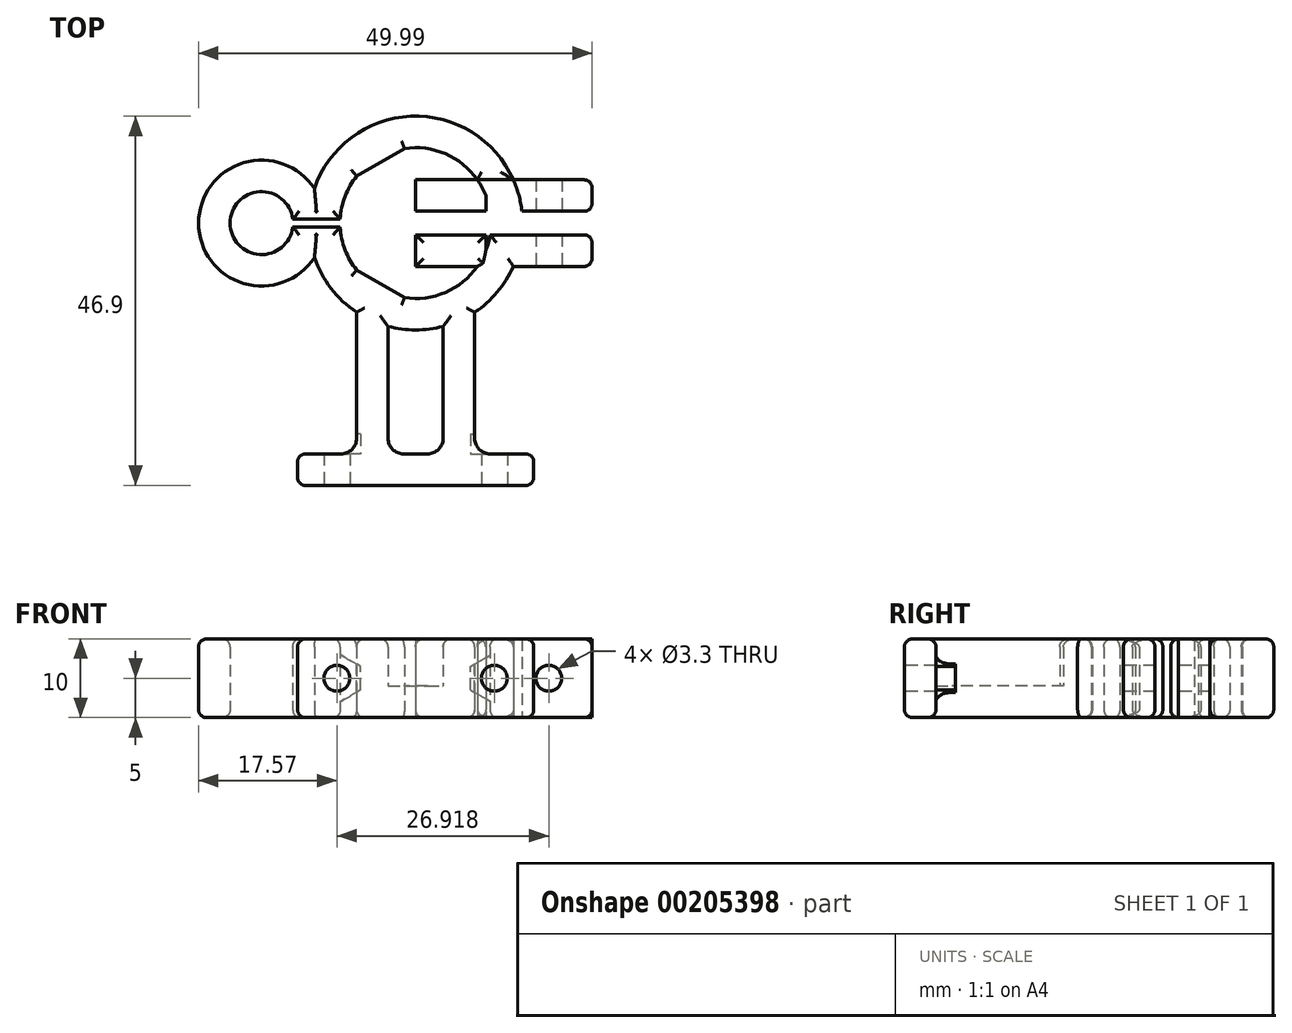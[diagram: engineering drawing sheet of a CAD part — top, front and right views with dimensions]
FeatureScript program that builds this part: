
annotation { "Feature Type Name" : "Feature", "Feature Type Description" : "" }
export const myFeature = defineFeature(function(context is Context, id is Id, definition is map)
    precondition{}
    {
        {
            assignVariable(context, id + "F0", {"name" : "wallWidth", "anyValue" : 4});
        }
        {
            assignVariable(context, id + "F1", {"name" : "height", "anyValue" : 10});
        }
        {
            var Q0;
            Q0=qCreatedBy(makeId("Top.planeOp"),FACE);
            var sketch = newSketch(context, id + "F2", { "sketchPlane" : qUnion([Q0])});
            skCircle(sketch, "E0", {"center": v(0, 0) * mm, "radius": 9.58 * mm});
            skPoint(sketch, "E1", {"position": v(0, 9.58) * mm});
            skPoint(sketch, "E2", {"position": v(-4.46, -7.72) * mm});
            skLineSegment(sketch, "E3", {"start": v(0, 9.58) * mm, "end": v(0, -8.92) * mm, "construction": true});
            skLineSegment(sketch, "E4.2.0", {"start": v(-7.5, -5.97) * mm, "end": v(-1.43, -9.47) * mm});
            skLineSegment(sketch, "E5.1.0", {"start": v(-1.43, 9.47) * mm, "end": v(-7.5, 5.97) * mm});
            skLineSegment(sketch, "E5.2.0", {"start": v(8.92, -3.5) * mm, "end": v(8.92, 3.5) * mm});
            skLineSegment(sketch, "E5.anchor1", {"start": v(0, 0) * mm, "end": v(-7.5, -5.97) * mm, "construction": true});
            skLineSegment(sketch, "E5.anchor2", {"start": v(0, 0) * mm, "end": v(8.92, -3.5) * mm, "construction": true});
            skCircle(sketch, "E6.0", {"center": v(0, 0) * mm, "radius": 13.58 * mm});
            skLineSegment(sketch, "E7.bottom", {"start": v(7.5, -11.32) * mm, "end": v(-7.5, -11.32) * mm});
            skLineSegment(sketch, "E7.top", {"start": v(1.5, -29.32) * mm, "end": v(-1.5, -29.32) * mm});
            skLineSegment(sketch, "E7.left", {"start": v(7.5, -11.32) * mm, "end": v(7.5, -27.32) * mm});
            skLineSegment(sketch, "E7.right", {"start": v(-7.5, -11.32) * mm, "end": v(-7.5, -27.32) * mm});
            skPoint(sketch, "E7.middle", {"position": v(0, -20.32) * mm});
            skLineSegment(sketch, "E8.bottom", {"start": v(-9.5, -29.32) * mm, "end": v(-14, -29.32) * mm});
            skLineSegment(sketch, "E8.top", {"start": v(14, -33.32) * mm, "end": v(-14, -33.32) * mm});
            skLineSegment(sketch, "E8.left", {"start": v(15, -30.32) * mm, "end": v(15, -32.32) * mm});
            skLineSegment(sketch, "E8.right", {"start": v(-15, -30.32) * mm, "end": v(-15, -32.32) * mm});
            skPoint(sketch, "E8.middle", {"position": v(0, -31.32) * mm});
            skPoint(sketch, "E9", {"position": v(0, -33.32) * mm});
            skLineSegment(sketch, "E10", {"start": v(0, -33.32) * mm, "end": v(10, -33.32) * mm});
            skLineSegment(sketch, "E11", {"start": v(0, -33.32) * mm, "end": v(-10, -33.32) * mm});
            skLineSegment(sketch, "E12", {"start": v(0, 0) * mm, "end": v(13.58, 0) * mm, "construction": true});
            skLineSegment(sketch, "E13.bottom", {"start": v(0, 0) * mm, "end": v(18.62, 0) * mm});
            skLineSegment(sketch, "E13.top", {"start": v(0, 1.5) * mm, "end": v(18.62, 1.5) * mm});
            skLineSegment(sketch, "E13.left", {"start": v(0, 0) * mm, "end": v(0, 1.5) * mm});
            skLineSegment(sketch, "E13.right", {"start": v(18.62, 0) * mm, "end": v(18.62, 1.5) * mm});
            skLineSegment(sketch, "E14.bottom", {"start": v(0, 0) * mm, "end": v(18.6, 0) * mm});
            skLineSegment(sketch, "E14.top", {"start": v(0, -1.5) * mm, "end": v(18.6, -1.5) * mm});
            skLineSegment(sketch, "E14.left", {"start": v(0, 0) * mm, "end": v(0, -1.5) * mm});
            skLineSegment(sketch, "E14.right", {"start": v(18.6, 0) * mm, "end": v(18.6, -1.5) * mm});
            skLineSegment(sketch, "E15.bottom", {"start": v(0, 1.5) * mm, "end": v(21.42, 1.5) * mm});
            skLineSegment(sketch, "E15.top", {"start": v(0, 5.5) * mm, "end": v(21.42, 5.5) * mm});
            skLineSegment(sketch, "E15.left", {"start": v(0, 1.5) * mm, "end": v(0, 5.5) * mm});
            skLineSegment(sketch, "E15.right", {"start": v(22.42, 2.5) * mm, "end": v(22.42, 4.5) * mm});
            skLineSegment(sketch, "E16.bottom", {"start": v(0, -1.5) * mm, "end": v(21.42, -1.5) * mm});
            skLineSegment(sketch, "E16.top", {"start": v(0, -5.5) * mm, "end": v(21.42, -5.5) * mm});
            skLineSegment(sketch, "E16.left", {"start": v(0, -1.5) * mm, "end": v(0, -5.5) * mm});
            skLineSegment(sketch, "E16.right", {"start": v(22.42, -2.5) * mm, "end": v(22.42, -4.5) * mm});
            skLineSegment(sketch, "E17", {"start": v(0, 0) * mm, "end": v(-19.57, 0) * mm, "construction": true});
            skCircle(sketch, "E18", {"center": v(-19.57, 0) * mm, "radius": 4 * mm});
            skCircle(sketch, "E19.0", {"center": v(-19.57, 0) * mm, "radius": 8 * mm});
            skLineSegment(sketch, "E20.left", {"start": v(-19.57, 8) * mm, "end": v(-19.57, 2.68) * mm});
            skLineSegment(sketch, "E21", {"start": v(-19.57, 0) * mm, "end": v(-19.57, 8) * mm, "construction": true});
            skLineSegment(sketch, "E22", {"start": v(3.5, -11.32) * mm, "end": v(3.5, -27.32) * mm});
            skLineSegment(sketch, "E23", {"start": v(-3.5, -11.32) * mm, "end": v(-3.5, -27.32) * mm});
            skLineSegment(sketch, "E24.top", {"start": v(-19.57, 0.5) * mm, "end": v(-9.57, 0.5) * mm});
            skLineSegment(sketch, "E24.right", {"start": v(-9.57, 0) * mm, "end": v(-9.57, 0.5) * mm});
            skLineSegment(sketch, "E25.top", {"start": v(-18.57, -0.5) * mm, "end": v(-9.57, -0.5) * mm});
            skLineSegment(sketch, "E25.right", {"start": v(-9.57, 0) * mm, "end": v(-9.57, -0.5) * mm});
            skPoint(sketch, "E26", {"position": v(-15.57, 0) * mm});
            skPoint(sketch, "E27.newPointB", {"position": v(15, -29.32) * mm});
            skLineSegment(sketch, "E28", {"start": v(14, -29.32) * mm, "end": v(9.5, -29.32) * mm});
            skPoint(sketch, "E29.visualSharp", {"position": v(7.5, -29.32) * mm});
            skArc(sketch, "E29.filletArc", {"start": v(7.5, -27.32) * mm, "mid": v(8.09, -28.74) * mm, "end": v(9.5, -29.32) * mm});
            skPoint(sketch, "E30.newPointA", {"position": v(3.5, -29.32) * mm});
            skArc(sketch, "E30.filletArc", {"start": v(1.5, -29.32) * mm, "mid": v(2.91, -28.74) * mm, "end": v(3.5, -27.32) * mm});
            skPoint(sketch, "E31.newPointA", {"position": v(-7.5, -29.32) * mm});
            skPoint(sketch, "E31.newPointB", {"position": v(-3.5, -29.32) * mm});
            skArc(sketch, "E31.filletArc", {"start": v(-3.5, -27.32) * mm, "mid": v(-2.91, -28.74) * mm, "end": v(-1.5, -29.32) * mm});
            skArc(sketch, "E32.filletArc", {"start": v(-9.5, -29.32) * mm, "mid": v(-8.09, -28.74) * mm, "end": v(-7.5, -27.32) * mm});
            skPoint(sketch, "E33.visualSharp", {"position": v(22.42, -1.5) * mm});
            skArc(sketch, "E33.filletArc", {"start": v(22.42, -2.5) * mm, "mid": v(22.12, -1.8) * mm, "end": v(21.42, -1.5) * mm});
            skPoint(sketch, "E34.visualSharp", {"position": v(22.42, 1.5) * mm});
            skArc(sketch, "E34.filletArc", {"start": v(21.42, 1.5) * mm, "mid": v(22.12, 1.8) * mm, "end": v(22.42, 2.5) * mm});
            skPoint(sketch, "E35.visualSharp", {"position": v(22.42, 5.5) * mm});
            skArc(sketch, "E35.filletArc", {"start": v(22.42, 4.5) * mm, "mid": v(22.12, 5.2) * mm, "end": v(21.42, 5.5) * mm});
            skPoint(sketch, "E36.visualSharp", {"position": v(22.42, -5.5) * mm});
            skArc(sketch, "E36.filletArc", {"start": v(21.42, -5.5) * mm, "mid": v(22.12, -5.2) * mm, "end": v(22.42, -4.5) * mm});
            skArc(sketch, "E37.filletArc", {"start": v(15, -30.32) * mm, "mid": v(14.7, -29.62) * mm, "end": v(14, -29.32) * mm});
            skPoint(sketch, "E38.visualSharp", {"position": v(15, -33.32) * mm});
            skArc(sketch, "E38.filletArc", {"start": v(14, -33.32) * mm, "mid": v(14.7, -33.03) * mm, "end": v(15, -32.32) * mm});
            skPoint(sketch, "E39", {"position": v(12.42, -5.5) * mm});
            skPoint(sketch, "E40", {"position": v(12.42, 5.5) * mm});
            skPoint(sketch, "E41.visualSharp", {"position": v(-15, -33.32) * mm});
            skArc(sketch, "E41.filletArc", {"start": v(-15, -32.32) * mm, "mid": v(-14.7, -33.03) * mm, "end": v(-14, -33.32) * mm});
            skPoint(sketch, "E42.visualSharp", {"position": v(-15, -29.32) * mm});
            skArc(sketch, "E42.filletArc", {"start": v(-14, -29.32) * mm, "mid": v(-14.7, -29.62) * mm, "end": v(-15, -30.32) * mm});
            skLineSegment(sketch, "E43", {"start": v(3.5, -29.32) * mm, "end": v(3.5, -27.32) * mm, "construction": true});
            skLineSegment(sketch, "E44", {"start": v(-3.5, -29.32) * mm, "end": v(-3.5, -27.32) * mm, "construction": true});
            skLineSegment(sketch, "E45", {"start": v(9.5, -29.32) * mm, "end": v(-9.5, -29.32) * mm, "construction": true});
            skLineSegment(sketch, "E46", {"start": v(7.5, -27.32) * mm, "end": v(7.5, -29.32) * mm, "construction": true});
            skSolve(sketch);
        }
        {
            var Q0;
            {var subQ6=sQuery(id+"F2.wireOp",EDGE,"E20.right");Q0=makeQuery(id+"F2.imprint","IMPRINT",FACE,{"disambiguationData":[TD([[makeQuery(id+"F2.imprint","IMPRINT",EDGE,{"derivedFrom":subQ6}),1.0]])]});}
            var Q1;
            {var subQ0=sQuery(id+"F2.wireOp",EDGE,"E15.bottom");var subQ1=sQuery(id+"F2.wireOp",EDGE,"E0");var subQ2=makeQuery(id+"F2.imprint","INTERSECT",VERTEX,{"derivedFrom":[subQ1,subQ0]});Q1=makeQuery(id+"F2.imprint","IMPRINT",FACE,{"disambiguationData":[TD([[makeQuery(id+"F2.imprint","IMPRINT",EDGE,{"disambiguationData":[TD([[subQ2,-1.0]])],"derivedFrom":subQ1}),-1.0]])]});}
            var Q2;
            {var subQ2=sQuery(id+"F2.wireOp",EDGE,"E15.right");Q2=makeQuery(id+"F2.imprint","IMPRINT",FACE,{"disambiguationData":[TD([[makeQuery(id+"F2.imprint","IMPRINT",EDGE,{"derivedFrom":subQ2}),1.0]])]});}
            var Q3;
            {var subQ0=sQuery(id+"F2.wireOp",EDGE,"E16.right");Q3=makeQuery(id+"F2.imprint","IMPRINT",FACE,{"disambiguationData":[TD([[makeQuery(id+"F2.imprint","IMPRINT",EDGE,{"derivedFrom":subQ0}),-1.0]])]});}
            var Q4;
            {var subQ0=sQuery(id+"F2.wireOp",EDGE,"E16.top");var subQ1=sQuery(id+"F2.wireOp",EDGE,"E0");var subQ2=makeQuery(id+"F2.imprint","INTERSECT",VERTEX,{"derivedFrom":[subQ1,subQ0]});Q4=makeQuery(id+"F2.imprint","IMPRINT",FACE,{"disambiguationData":[TD([[makeQuery(id+"F2.imprint","IMPRINT",EDGE,{"disambiguationData":[TD([[subQ2,-1.0]])],"derivedFrom":subQ1}),-1.0]])]});}
            var Q5;
            {var subQ0=sQuery(id+"F2.wireOp",EDGE,"vKI5tk8C-QuSu-6IvA-wCT6-3tnONTHLCrgP.right");Q5=makeQuery(id+"F2.imprint","IMPRINT",FACE,{"disambiguationData":[TD([[makeQuery(id+"F2.imprint","IMPRINT",EDGE,{"derivedFrom":subQ0}),1.0]])]});}
            var Q6;
            {var subQ0=sQuery(id+"F2.wireOp",EDGE,"E20.right");Q6=makeQuery(id+"F2.imprint","IMPRINT",FACE,{"disambiguationData":[TD([[makeQuery(id+"F2.imprint","IMPRINT",EDGE,{"derivedFrom":subQ0}),-1.0]])]});}
            var Q7;
            {var subQ0=sQuery(id+"F2.wireOp",EDGE,"vKI5tk8C-QuSu-6IvA-wCT6-3tnONTHLCrgP.right");Q7=makeQuery(id+"F2.imprint","IMPRINT",FACE,{"disambiguationData":[TD([[makeQuery(id+"F2.imprint","IMPRINT",EDGE,{"derivedFrom":subQ0}),-1.0]])]});}
            var Q8;
            {var subQ0=sQuery(id+"F2.wireOp",EDGE,"E5.1.0");Q8=makeQuery(id+"F2.imprint","IMPRINT",FACE,{"disambiguationData":[TD([[makeQuery(id+"F2.imprint","IMPRINT",EDGE,{"derivedFrom":subQ0}),-1.0]])]});}
            var Q9;
            {var subQ0=sQuery(id+"F2.wireOp",EDGE,"E15.bottom");var subQ1=sQuery(id+"F2.wireOp",EDGE,"E0");var subQ2=makeQuery(id+"F2.imprint","INTERSECT",VERTEX,{"derivedFrom":[subQ1,subQ0]});Q9=makeQuery(id+"F2.imprint","IMPRINT",FACE,{"disambiguationData":[TD([[makeQuery(id+"F2.imprint","IMPRINT",EDGE,{"disambiguationData":[TD([[subQ2,-1.0]])],"derivedFrom":subQ1}),1.0]])]});}
            var Q10;
            {var subQ0=sQuery(id+"F2.wireOp",EDGE,"E5.2.0");var subQ1=sQuery(id+"F2.wireOp",EDGE,"E0");var subQ2=makeQuery(id+"F2.imprint","INTERSECT",VERTEX,{"disambiguationData":[OD(1.0)],"derivedFrom":[subQ1,subQ0]});Q10=makeQuery(id+"F2.imprint","IMPRINT",FACE,{"disambiguationData":[TD([[makeQuery(id+"F2.imprint","IMPRINT",EDGE,{"disambiguationData":[TD([[subQ2,1.0]])],"derivedFrom":subQ1}),1.0]])]});}
            var Q11;
            {var subQ0=sQuery(id+"F2.wireOp",EDGE,"E4.2.0");Q11=makeQuery(id+"F2.imprint","IMPRINT",FACE,{"disambiguationData":[TD([[makeQuery(id+"F2.imprint","IMPRINT",EDGE,{"derivedFrom":subQ0}),-1.0]])]});}
            var Q12;
            {var subQ0=sQuery(id+"F2.wireOp",EDGE,"E7.bottom");var subQ3=sQuery(id+"F2.wireOp",EDGE,"E22");var subQ5=makeQuery(id+"F2.imprint","INTERSECT",VERTEX,{"derivedFrom":[subQ0,subQ3]});Q12=makeQuery(id+"F2.imprint","IMPRINT",FACE,{"disambiguationData":[TD([[makeQuery(id+"F2.imprint","IMPRINT",EDGE,{"disambiguationData":[TD([[subQ5,-1.0]])],"derivedFrom":subQ3}),1.0]])]});}
            var Q13;
            {var subQ0=sQuery(id+"F2.wireOp",EDGE,"E23");var subQ1=sQuery(id+"F2.wireOp",EDGE,"E6.0");var subQ2=makeQuery(id+"F2.imprint","INTERSECT",VERTEX,{"derivedFrom":[subQ1,subQ0]});Q13=makeQuery(id+"F2.imprint","IMPRINT",FACE,{"disambiguationData":[TD([[makeQuery(id+"F2.imprint","IMPRINT",EDGE,{"disambiguationData":[TD([[subQ2,-1.0]])],"derivedFrom":subQ1}),1.0]])]});}
            var Q14;
            {var subQ0=sQuery(id+"F2.wireOp",EDGE,"E23");var subQ1=sQuery(id+"F2.wireOp",EDGE,"E6.0");var subQ2=makeQuery(id+"F2.imprint","INTERSECT",VERTEX,{"derivedFrom":[subQ1,subQ0]});Q14=makeQuery(id+"F2.imprint","IMPRINT",FACE,{"disambiguationData":[TD([[makeQuery(id+"F2.imprint","IMPRINT",EDGE,{"disambiguationData":[TD([[subQ2,-1.0]])],"derivedFrom":subQ1}),1.0]])]});}
            var Q15;
            {var subQ0=sQuery(id+"F2.wireOp",EDGE,"E7.bottom");var subQ3=sQuery(id+"F2.wireOp",EDGE,"E23");var subQ5=makeQuery(id+"F2.imprint","INTERSECT",VERTEX,{"derivedFrom":[subQ0,subQ3]});Q15=makeQuery(id+"F2.imprint","IMPRINT",FACE,{"disambiguationData":[TD([[makeQuery(id+"F2.imprint","IMPRINT",EDGE,{"disambiguationData":[TD([[subQ5,-1.0]])],"derivedFrom":subQ3}),-1.0]])]});}
            var Q16;
            {var subQ4=sQuery(id+"F2.wireOp",EDGE,"E7.left");Q16=makeQuery(id+"F2.imprint","IMPRINT",FACE,{"disambiguationData":[TD([[makeQuery(id+"F2.imprint","IMPRINT",EDGE,{"derivedFrom":subQ4}),-1.0]])]});}
            var Q17;
            {var subQ4=sQuery(id+"F2.wireOp",EDGE,"E7.right");Q17=makeQuery(id+"F2.imprint","IMPRINT",FACE,{"disambiguationData":[TD([[makeQuery(id+"F2.imprint","IMPRINT",EDGE,{"derivedFrom":subQ4}),1.0]])]});}
            var Q18;
            Q18=makeQuery(id+"F2.imprint","IMPRINT",FACE,{"disambiguationData":[TD([[makeQuery(id+"F2.imprint","IMPRINT",EDGE,{"derivedFrom":sQuery(id+"F2.wireOp",EDGE,"hK8FCwQg-aAdL-F7ev-FIwV-hXwe2HGtbRtO.bottom")}),-1.0]])]});
            var Q19;
            Q19=makeQuery(id+"F2.imprint","IMPRINT",FACE,{"disambiguationData":[TD([[makeQuery(id+"F2.imprint","IMPRINT",EDGE,{"derivedFrom":sQuery(id+"F2.wireOp",EDGE,"mCSpb51D-tCi6-9t4P-GL09-24iLFyGQ1Y56.bottom")}),1.0]])]});
            var Q20;
            {var subQ7=sQuery(id+"F2.wireOp",EDGE,"E8.left");Q20=makeQuery(id+"F2.imprint","IMPRINT",FACE,{"disambiguationData":[TD([[makeQuery(id+"F2.imprint","IMPRINT",EDGE,{"derivedFrom":subQ7}),-1.0]])]});}
            var Q21;
            {var subQ7=sQuery(id+"F2.wireOp",EDGE,"E8.left");Q21=makeQuery(id+"F2.imprint","IMPRINT",FACE,{"disambiguationData":[TD([[makeQuery(id+"F2.imprint","IMPRINT",EDGE,{"derivedFrom":subQ7}),-1.0]])]});}
            var Q22;
            {var subQ12=sQuery(id+"F2.wireOp",EDGE,"E0");var subQ14=sQuery(id+"F2.wireOp",EDGE,"E4.2.0");var subQ15=makeQuery(id+"F2.imprint","INTERSECT",VERTEX,{"disambiguationData":[OD(0.0)],"derivedFrom":[subQ12,subQ14]});Q22=makeQuery(id+"F2.imprint","IMPRINT",FACE,{"disambiguationData":[TD([[makeQuery(id+"F2.imprint","IMPRINT",EDGE,{"disambiguationData":[TD([[subQ15,-1.0]])],"derivedFrom":subQ12}),-1.0]])]});}
            var Q23;
            {var subQ0=sQuery(id+"F2.wireOp",EDGE,"E19.0");var subQ1=sQuery(id+"F2.wireOp",EDGE,"E6.0");var subQ2=makeQuery(id+"F2.imprint","INTERSECT",VERTEX,{"disambiguationData":[OD(1.0)],"derivedFrom":[subQ1,subQ0]});Q23=makeQuery(id+"F2.imprint","IMPRINT",FACE,{"disambiguationData":[TD([[makeQuery(id+"F2.imprint","IMPRINT",EDGE,{"disambiguationData":[TD([[subQ2,1.0]])],"derivedFrom":subQ1}),1.0]])]});}
            var Q24;
            {var subQ0=sQuery(id+"F2.wireOp",EDGE,"E19.0");var subQ1=sQuery(id+"F2.wireOp",EDGE,"E6.0");var subQ2=makeQuery(id+"F2.imprint","INTERSECT",VERTEX,{"disambiguationData":[OD(0.0)],"derivedFrom":[subQ1,subQ0]});Q24=makeQuery(id+"F2.imprint","IMPRINT",FACE,{"disambiguationData":[TD([[makeQuery(id+"F2.imprint","IMPRINT",EDGE,{"disambiguationData":[TD([[subQ2,-1.0]])],"derivedFrom":subQ1}),1.0]])]});}
            var Q25;
            {var subQ1=sQuery(id+"F2.wireOp",EDGE,"E19.0");var subQ7=sQuery(id+"F2.wireOp",EDGE,"E6.0");var subQ8=makeQuery(id+"F2.imprint","INTERSECT",VERTEX,{"disambiguationData":[OD(0.0)],"derivedFrom":[subQ7,subQ1]});Q25=makeQuery(id+"F2.imprint","IMPRINT",FACE,{"disambiguationData":[TD([[makeQuery(id+"F2.imprint","IMPRINT",EDGE,{"disambiguationData":[TD([[subQ8,-1.0]])],"derivedFrom":subQ7}),-1.0]])]});}
            var Q26;
            {var subQ1=sQuery(id+"F2.wireOp",EDGE,"E19.0");var subQ3=sQuery(id+"F2.wireOp",EDGE,"E6.0");var subQ4=makeQuery(id+"F2.imprint","INTERSECT",VERTEX,{"disambiguationData":[OD(1.0)],"derivedFrom":[subQ3,subQ1]});Q26=makeQuery(id+"F2.imprint","IMPRINT",FACE,{"disambiguationData":[TD([[makeQuery(id+"F2.imprint","IMPRINT",EDGE,{"disambiguationData":[TD([[subQ4,1.0]])],"derivedFrom":subQ3}),-1.0]])]});}
            var Q27;
            {var subQ1=sQuery(id+"F2.wireOp",EDGE,"E0");var subQ12=makeQuery(id+"F2.imprint","INTERSECT",VERTEX,{"disambiguationData":[OD(1.0)],"derivedFrom":[subQ1,sQuery(id+"F2.wireOp",EDGE,"E5.2.0")]});Q27=makeQuery(id+"F2.imprint","IMPRINT",FACE,{"disambiguationData":[TD([[makeQuery(id+"F2.imprint","IMPRINT",EDGE,{"disambiguationData":[TD([[subQ12,1.0]])],"derivedFrom":subQ1}),-1.0]])]});}
            var Q28;
            {var subQ7=sQuery(id+"F2.wireOp",EDGE,"E5.1.0");var subQ8=sQuery(id+"F2.wireOp",EDGE,"E0");var subQ11=makeQuery(id+"F2.imprint","INTERSECT",VERTEX,{"disambiguationData":[OD(0.0)],"derivedFrom":[subQ8,subQ7]});Q28=makeQuery(id+"F2.imprint","IMPRINT",FACE,{"disambiguationData":[TD([[makeQuery(id+"F2.imprint","IMPRINT",EDGE,{"disambiguationData":[TD([[subQ11,1.0]])],"derivedFrom":subQ8}),-1.0]])]});}
            var Q29;
            {var subQ0=sQuery(id+"F2.wireOp",EDGE,"E5.2.0");var subQ1=sQuery(id+"F2.wireOp",EDGE,"E0");var subQ2=makeQuery(id+"F2.imprint","INTERSECT",VERTEX,{"disambiguationData":[OD(0.0)],"derivedFrom":[subQ1,subQ0]});Q29=makeQuery(id+"F2.imprint","IMPRINT",FACE,{"disambiguationData":[TD([[makeQuery(id+"F2.imprint","IMPRINT",EDGE,{"disambiguationData":[TD([[subQ2,-1.0]])],"derivedFrom":subQ1}),1.0]])]});}
            extrude(context, id + "F3", {"entities" : qUnion([Q0, Q1, Q2, Q3, Q4, Q5, Q6, Q7, Q8, Q9, Q10, Q11, Q12, Q13, Q14, Q15, Q16, Q17, Q18, Q19, Q20, Q21, Q22, Q23, Q24, Q25, Q26, Q27, Q28, Q29]), "depth" : (getVariable(context, 'height')) * mm});
        }
        {
            var Q0;
            Q0=makeQuery(id+"F3.opExtrude","SWEPT_FACE",FACE,{"disambiguationData":[OSD([sQuery(id+"F2.wireOp",EDGE,"E8.top"),sQuery(id+"F2.wireOp",EDGE,"E10"),sQuery(id+"F2.wireOp",EDGE,"E11")])]});
            var sketch = newSketch(context, id + "F4", { "sketchPlane" : qUnion([Q0])});
            skLineSegment(sketch, "E47.0", {"start": v(0, 0) * mm, "end": v(-10, 0) * mm});
            skLineSegment(sketch, "E47.1", {"start": v(0, 0) * mm, "end": v(10, 0) * mm});
            skLineSegment(sketch, "E47.2", {"start": v(14, 10) * mm, "end": v(14, 10) * mm});
            skPoint(sketch, "E47.6", {"position": v(-3.5, 0) * mm});
            skPoint(sketch, "E47.7", {"position": v(3.5, 0) * mm});
            skPoint(sketch, "E47.8", {"position": v(7.5, 0) * mm});
            skLineSegment(sketch, "E48", {"start": v(10, 0) * mm, "end": v(10, 10) * mm, "construction": true});
            skLineSegment(sketch, "E49", {"start": v(-10, 0) * mm, "end": v(-10, 10) * mm, "construction": true});
            skCircle(sketch, "E50", {"center": v(-10, 5) * mm, "radius": 1.65 * mm});
            skCircle(sketch, "E51", {"center": v(10, 5) * mm, "radius": 1.65 * mm});
            skLineSegment(sketch, "E52", {"start": v(-10, 5) * mm, "end": v(10, 5) * mm, "construction": true});
            skPoint(sketch, "E53.0", {"position": v(14, 0) * mm});
            skLineSegment(sketch, "E54", {"start": v(14, 0) * mm, "end": v(14, 10) * mm});
            skSolve(sketch);
        }
        {
            var Q0;
            Q0=makeQuery(id+"F4.imprint","IMPRINT",FACE,{"disambiguationData":[TD([[makeQuery(id+"F4.imprint","IMPRINT",EDGE,{"derivedFrom":sQuery(id+"F4.wireOp",EDGE,"E50")}),1.0]])]});
            var Q1;
            Q1=makeQuery(id+"F4.imprint","IMPRINT",FACE,{"disambiguationData":[TD([[makeQuery(id+"F4.imprint","IMPRINT",EDGE,{"derivedFrom":sQuery(id+"F4.wireOp",EDGE,"E51")}),1.0]])]});
            extrude(context, id + "F5", {"entities" : qUnion([Q0, Q1]), "operationType" : NewBodyOperationType.REMOVE, "endBound" : BoundingType.UP_TO_NEXT, "oppositeDirection" : true, "depth" : 25 * mm});
        }
        {
            var Q0;
            {var subQ0=sQuery(id+"F2.wireOp",EDGE,"E8.bottom");Q0=makeQuery(id+"F3.opExtrude","SWEPT_FACE",FACE,{"disambiguationData":[OSD([subQ0]),TDD([makeQuery(id+"F2.imprint","IMPRINT",EDGE,{"disambiguationData":[TD([[makeQuery(id+"F2.imprint","INTERSECT",VERTEX,{"derivedFrom":[subQ0,sQuery(id+"F2.wireOp",EDGE,"E8.right")]}),1.0]])],"derivedFrom":subQ0})])]});}
            var sketch = newSketch(context, id + "F6", { "sketchPlane" : qUnion([Q0])});
            skPoint(sketch, "E55.0", {"position": v(10, 5) * mm});
            skCircle(sketch, "E56.0", {"center": v(10, 5) * mm, "radius": 1.65 * mm});
            skLineSegment(sketch, "E57.0", {"start": v(10, 5) * mm, "end": v(-10, 5) * mm, "construction": true});
            skLineSegment(sketch, "E58.0", {"start": v(10, 0) * mm, "end": v(10, 10) * mm});
            skLineSegment(sketch, "E59.0", {"start": v(-10, 0) * mm, "end": v(-10, 10) * mm});
            skCircle(sketch, "E60.0", {"center": v(-10, 5) * mm, "radius": 1.65 * mm});
            skLineSegment(sketch, "E61.0", {"start": v(14, 0) * mm, "end": v(14, 10) * mm, "construction": true});
            skLineSegment(sketch, "E62", {"start": v(7, 3.5) * mm, "end": v(7, 6.5) * mm});
            skPoint(sketch, "E63", {"position": v(7, 5) * mm});
            skLineSegment(sketch, "E64", {"start": v(7, 6.5) * mm, "end": v(10, 8.23) * mm});
            skLineSegment(sketch, "E65", {"start": v(7, 3.5) * mm, "end": v(10, 1.77) * mm});
            skPoint(sketch, "E66", {"position": v(14, 5) * mm});
            skLineSegment(sketch, "E67", {"start": v(0, 0) * mm, "end": v(0, 10) * mm, "construction": true});
            skLineSegment(sketch, "E68.MirrorCS", {"start": v(-7, 3.5) * mm, "end": v(-10, 1.77) * mm});
            skLineSegment(sketch, "E69.MirrorCS", {"start": v(-7, 3.5) * mm, "end": v(-7, 6.5) * mm});
            skLineSegment(sketch, "E70.MirrorCS", {"start": v(-7, 6.5) * mm, "end": v(-10, 8.23) * mm});
            skPoint(sketch, "E71.MirrorP", {"position": v(-14, 5) * mm});
            skPoint(sketch, "E72.MirrorP", {"position": v(-7, 5) * mm});
            skLineSegment(sketch, "E73.0", {"start": v(7.5, 10) * mm, "end": v(7.5, 0) * mm});
            skLineSegment(sketch, "E74.0", {"start": v(-3.5, 10) * mm, "end": v(-3.5, 0) * mm, "construction": true});
            skLineSegment(sketch, "E75.0", {"start": v(3.5, 10) * mm, "end": v(3.5, 0) * mm, "construction": true});
            skLineSegment(sketch, "E76.0", {"start": v(-7.5, 10) * mm, "end": v(-7.5, 0) * mm});
            skPoint(sketch, "E77.0", {"position": v(7.5, 0) * mm});
            skPoint(sketch, "E78.0", {"position": v(3.5, 0) * mm});
            skPoint(sketch, "E79.0", {"position": v(-3.5, 0) * mm});
            skPoint(sketch, "E80.0", {"position": v(-7.5, 0) * mm});
            skLineSegment(sketch, "E81.0", {"start": v(-9.5, 0) * mm, "end": v(9.5, 0) * mm, "construction": true});
            skLineSegment(sketch, "E82", {"start": v(14, 10) * mm, "end": v(-10, 10) * mm, "construction": true});
            skPoint(sketch, "E83", {"position": v(10, 6.65) * mm});
            skPoint(sketch, "E84", {"position": v(10, 3.35) * mm});
            skPoint(sketch, "E85", {"position": v(-10, 6.65) * mm});
            skPoint(sketch, "E86", {"position": v(-10, 3.35) * mm});
            skSolve(sketch);
        }
        {
            var Q0;
            {var subQ5=sQuery(id+"F6.wireOp",EDGE,"E68.MirrorCS");Q0=makeQuery(id+"F6.imprint","IMPRINT",FACE,{"disambiguationData":[TD([[makeQuery(id+"F6.imprint","IMPRINT",EDGE,{"derivedFrom":subQ5}),-1.0]])]});}
            var Q1;
            {var subQ5=sQuery(id+"F6.wireOp",EDGE,"E70.MirrorCS");Q1=makeQuery(id+"F6.imprint","IMPRINT",FACE,{"disambiguationData":[TD([[makeQuery(id+"F6.imprint","IMPRINT",EDGE,{"derivedFrom":subQ5}),1.0]])]});}
            var Q2;
            {var subQ5=sQuery(id+"F6.wireOp",EDGE,"E65");Q2=makeQuery(id+"F6.imprint","IMPRINT",FACE,{"disambiguationData":[TD([[makeQuery(id+"F6.imprint","IMPRINT",EDGE,{"derivedFrom":subQ5}),1.0]])]});}
            var Q3;
            {var subQ5=sQuery(id+"F6.wireOp",EDGE,"E64");Q3=makeQuery(id+"F6.imprint","IMPRINT",FACE,{"disambiguationData":[TD([[makeQuery(id+"F6.imprint","IMPRINT",EDGE,{"derivedFrom":subQ5}),-1.0]])]});}
            var Q4;
            {var subQ0=sQuery(id+"F6.wireOp",EDGE,"E73.0");var subQ1=sQuery(id+"F6.wireOp",EDGE,"E64");var subQ2=makeQuery(id+"F6.imprint","INTERSECT",VERTEX,{"derivedFrom":[subQ1,subQ0]});Q4=makeQuery(id+"F6.imprint","IMPRINT",FACE,{"disambiguationData":[TD([[makeQuery(id+"F6.imprint","IMPRINT",EDGE,{"disambiguationData":[TD([[subQ2,-1.0]])],"derivedFrom":subQ0}),1.0]])]});}
            var Q5;
            {var subQ0=sQuery(id+"F6.wireOp",EDGE,"E68.MirrorCS");var subQ1=sQuery(id+"F6.wireOp",EDGE,"E59.0");var subQ2=makeQuery(id+"F6.imprint","INTERSECT",VERTEX,{"derivedFrom":[subQ1,subQ0]});Q5=makeQuery(id+"F6.imprint","IMPRINT",FACE,{"disambiguationData":[TD([[makeQuery(id+"F6.imprint","IMPRINT",EDGE,{"disambiguationData":[TD([[subQ2,-1.0]])],"derivedFrom":subQ1}),-1.0]])]});}
            extrude(context, id + "F7", {"entities" : qUnion([Q0, Q1, Q2, Q3, Q4, Q5]), "operationType" : NewBodyOperationType.REMOVE, "depth" : 2.5 * mm});
        }
        {
            var Q0;
            Q0=makeQuery(id+"F3.opExtrude","SWEPT_FACE",FACE,{"disambiguationData":[OSD([sQuery(id+"F2.wireOp",EDGE,"E16.top")])]});
            var sketch = newSketch(context, id + "F8", { "sketchPlane" : qUnion([Q0])});
            skLineSegment(sketch, "E87", {"start": v(16.92, 0) * mm, "end": v(16.92, 10) * mm, "construction": true});
            skLineSegment(sketch, "E88", {"start": v(21.42, 5) * mm, "end": v(12.42, 5) * mm, "construction": true});
            skPoint(sketch, "E89", {"position": v(16.92, 5) * mm});
            skCircle(sketch, "E90", {"center": v(16.92, 5) * mm, "radius": 1.65 * mm});
            skLineSegment(sketch, "E91.0", {"start": v(21.42, 10) * mm, "end": v(21.42, 0) * mm});
            skLineSegment(sketch, "E92.0", {"start": v(12.42, 10) * mm, "end": v(12.42, 0) * mm});
            skSolve(sketch);
        }
        {
            var Q0;
            Q0=makeQuery(id+"F8.imprint","IMPRINT",FACE,{"disambiguationData":[TD([[makeQuery(id+"F8.imprint","IMPRINT",EDGE,{"derivedFrom":sQuery(id+"F8.wireOp",EDGE,"E90")}),1.0]])]});
            var Q1;
            Q1=makeQuery(id+"F3.opExtrude","SWEPT_FACE",FACE,{"disambiguationData":[OSD([sQuery(id+"F2.wireOp",EDGE,"E15.top")])]});
            extrude(context, id + "F9", {"entities" : qUnion([Q0]), "operationType" : NewBodyOperationType.REMOVE, "endBound" : BoundingType.UP_TO_SURFACE, "oppositeDirection" : true, "endBoundEntityFace" : qUnion([Q1]), "depth" : 25 * mm});
        }
        {
            var Q0;
            {var subQ0=sQuery(id+"F2.wireOp",EDGE,"E23");var subQ1=sQuery(id+"F2.wireOp",EDGE,"E6.0");var subQ2=makeQuery(id+"F2.imprint","INTERSECT",VERTEX,{"derivedFrom":[subQ1,subQ0]});Q0=makeQuery(id+"F2.imprint","IMPRINT",FACE,{"disambiguationData":[TD([[makeQuery(id+"F2.imprint","IMPRINT",EDGE,{"disambiguationData":[TD([[subQ2,-1.0]])],"derivedFrom":subQ1}),-1.0]])]});}
            extrude(context, id + "F10", {"entities" : qUnion([Q0]), "operationType" : NewBodyOperationType.ADD, "depth" : (getVariable(context, 'wallWidth')) * mm});
        }
        {
            var Q0;
            {var subQ0=sQuery(id+"F2.wireOp",EDGE,"E31.filletArc");var subQ1=sQuery(id+"F2.wireOp",EDGE,"E30.filletArc");var subQ2=sQuery(id+"F2.wireOp",EDGE,"E23");var subQ3=sQuery(id+"F2.wireOp",EDGE,"E22");var subQ4=sQuery(id+"F2.wireOp",EDGE,"E7.top");var subQ5=sQuery(id+"F2.wireOp",EDGE,"E6.0");Q0=makeQuery(id+"F10.boolean.opBoolean","MERGE",FACE,{"derivedFrom":[makeQuery(id+"F3.opExtrude","CAP_FACE",FACE,{"disambiguationData":[OSD([sQuery(id+"F2.wireOp",EDGE,"E0"),sQuery(id+"F2.wireOp",EDGE,"E4.2.0"),sQuery(id+"F2.wireOp",EDGE,"E5.1.0"),sQuery(id+"F2.wireOp",EDGE,"E5.2.0"),subQ5,subQ4,sQuery(id+"F2.wireOp",EDGE,"E7.left"),sQuery(id+"F2.wireOp",EDGE,"E7.right"),sQuery(id+"F2.wireOp",EDGE,"E8.bottom"),sQuery(id+"F2.wireOp",EDGE,"E8.top"),sQuery(id+"F2.wireOp",EDGE,"E8.left"),sQuery(id+"F2.wireOp",EDGE,"E8.right"),sQuery(id+"F2.wireOp",EDGE,"E10"),sQuery(id+"F2.wireOp",EDGE,"E11"),sQuery(id+"F2.wireOp",EDGE,"E15.bottom"),sQuery(id+"F2.wireOp",EDGE,"E15.top"),sQuery(id+"F2.wireOp",EDGE,"E15.right"),sQuery(id+"F2.wireOp",EDGE,"E16.bottom"),sQuery(id+"F2.wireOp",EDGE,"E16.top"),sQuery(id+"F2.wireOp",EDGE,"E16.right"),sQuery(id+"F2.wireOp",EDGE,"E18"),sQuery(id+"F2.wireOp",EDGE,"E19.0"),subQ3,subQ2,sQuery(id+"F2.wireOp",EDGE,"E24.top"),sQuery(id+"F2.wireOp",EDGE,"E25.top"),sQuery(id+"F2.wireOp",EDGE,"E28"),sQuery(id+"F2.wireOp",EDGE,"E29.filletArc"),subQ1,subQ0,sQuery(id+"F2.wireOp",EDGE,"E32.filletArc"),sQuery(id+"F2.wireOp",EDGE,"E33.filletArc"),sQuery(id+"F2.wireOp",EDGE,"E34.filletArc"),sQuery(id+"F2.wireOp",EDGE,"E35.filletArc"),sQuery(id+"F2.wireOp",EDGE,"E36.filletArc"),sQuery(id+"F2.wireOp",EDGE,"E37.filletArc"),sQuery(id+"F2.wireOp",EDGE,"E38.filletArc"),sQuery(id+"F2.wireOp",EDGE,"E41.filletArc"),sQuery(id+"F2.wireOp",EDGE,"E42.filletArc")])],"isStart":true}),makeQuery(id+"F10.opExtrude","CAP_FACE",FACE,{"disambiguationData":[OSD([subQ5,subQ4,subQ3,subQ2,subQ1,subQ0])],"isStart":true})]});}
            fillet(context, id + "F11", {"entities" : qUnion([Q0]), "radius" : 1 * mm, "tangentPropagation" : true, "allowEdgeOverflow" : false});
        }
        {
            var Q0;
            Q0=makeQuery(id+"F3.opExtrude","CAP_FACE",FACE,{"disambiguationData":[OSD([sQuery(id+"F2.wireOp",EDGE,"E0"),sQuery(id+"F2.wireOp",EDGE,"E4.2.0"),sQuery(id+"F2.wireOp",EDGE,"E5.1.0"),sQuery(id+"F2.wireOp",EDGE,"E5.2.0"),sQuery(id+"F2.wireOp",EDGE,"E6.0"),sQuery(id+"F2.wireOp",EDGE,"E7.top"),sQuery(id+"F2.wireOp",EDGE,"E7.left"),sQuery(id+"F2.wireOp",EDGE,"E7.right"),sQuery(id+"F2.wireOp",EDGE,"E8.bottom"),sQuery(id+"F2.wireOp",EDGE,"E8.top"),sQuery(id+"F2.wireOp",EDGE,"E8.left"),sQuery(id+"F2.wireOp",EDGE,"E8.right"),sQuery(id+"F2.wireOp",EDGE,"E10"),sQuery(id+"F2.wireOp",EDGE,"E11"),sQuery(id+"F2.wireOp",EDGE,"E15.bottom"),sQuery(id+"F2.wireOp",EDGE,"E15.top"),sQuery(id+"F2.wireOp",EDGE,"E15.right"),sQuery(id+"F2.wireOp",EDGE,"E16.bottom"),sQuery(id+"F2.wireOp",EDGE,"E16.top"),sQuery(id+"F2.wireOp",EDGE,"E16.right"),sQuery(id+"F2.wireOp",EDGE,"E18"),sQuery(id+"F2.wireOp",EDGE,"E19.0"),sQuery(id+"F2.wireOp",EDGE,"E22"),sQuery(id+"F2.wireOp",EDGE,"E23"),sQuery(id+"F2.wireOp",EDGE,"E24.top"),sQuery(id+"F2.wireOp",EDGE,"E25.top"),sQuery(id+"F2.wireOp",EDGE,"E28"),sQuery(id+"F2.wireOp",EDGE,"E29.filletArc"),sQuery(id+"F2.wireOp",EDGE,"E30.filletArc"),sQuery(id+"F2.wireOp",EDGE,"E31.filletArc"),sQuery(id+"F2.wireOp",EDGE,"E32.filletArc"),sQuery(id+"F2.wireOp",EDGE,"E33.filletArc"),sQuery(id+"F2.wireOp",EDGE,"E34.filletArc"),sQuery(id+"F2.wireOp",EDGE,"E35.filletArc"),sQuery(id+"F2.wireOp",EDGE,"E36.filletArc"),sQuery(id+"F2.wireOp",EDGE,"E37.filletArc"),sQuery(id+"F2.wireOp",EDGE,"E38.filletArc"),sQuery(id+"F2.wireOp",EDGE,"E41.filletArc"),sQuery(id+"F2.wireOp",EDGE,"E42.filletArc")])],"isStart":false});
            fillet(context, id + "F12", {"entities" : qUnion([Q0]), "radius" : 1 * mm, "tangentPropagation" : true, "allowEdgeOverflow" : false});
        }
    });
